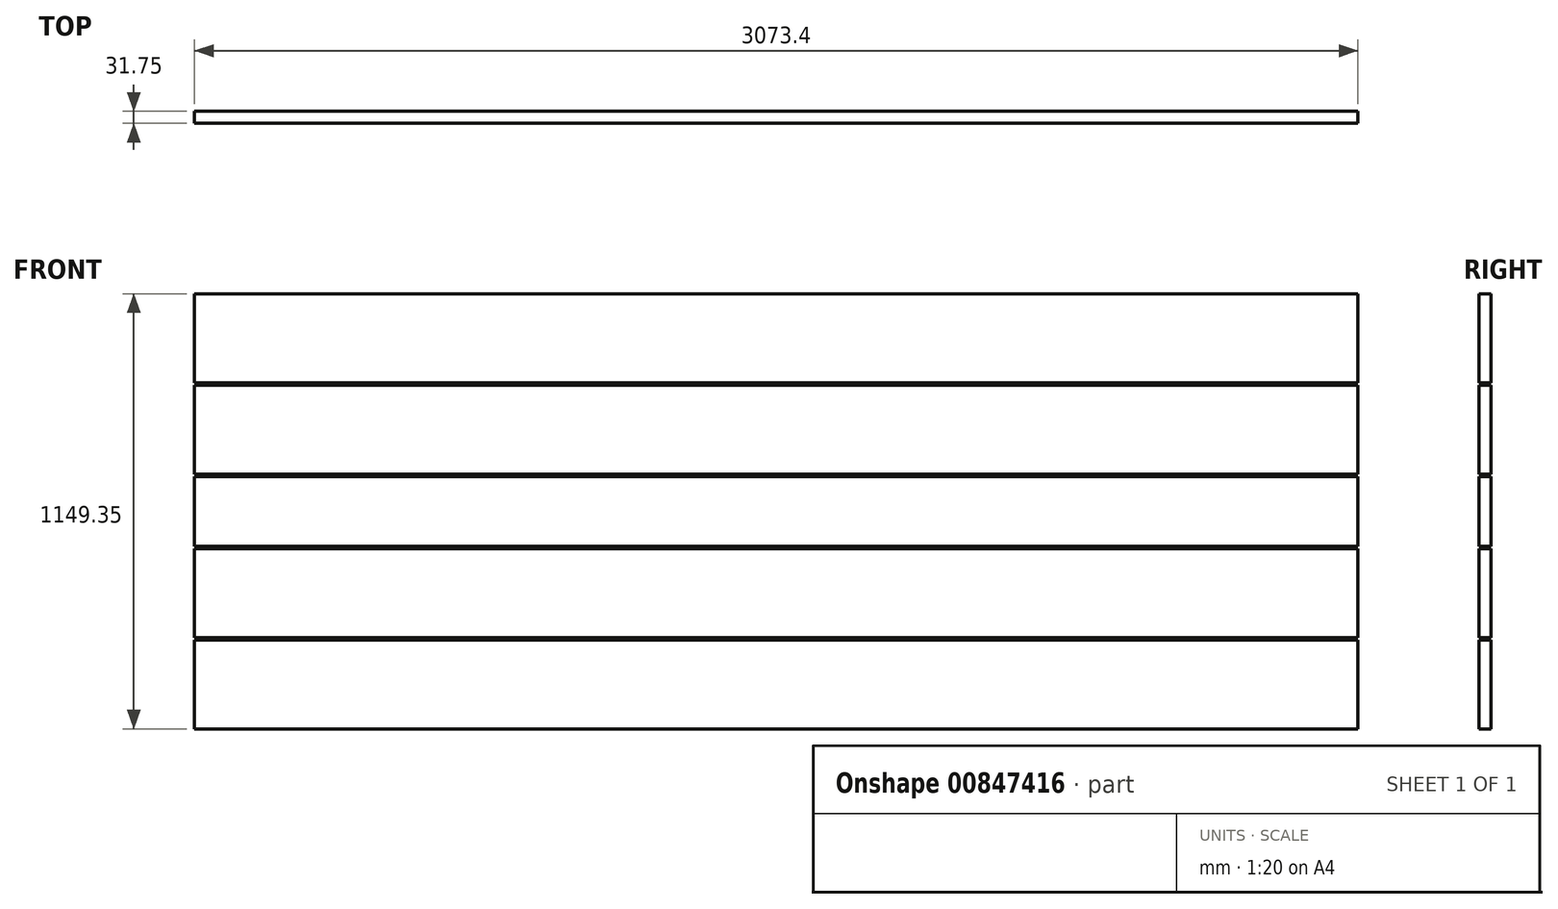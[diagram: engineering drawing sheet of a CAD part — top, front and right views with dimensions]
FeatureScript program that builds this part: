
annotation { "Feature Type Name" : "Feature", "Feature Type Description" : "" }
export const myFeature = defineFeature(function(context is Context, id is Id, definition is map)
    precondition{}
    {
        {
            var Q0;
            Q0=qCreatedBy(makeId("Front.planeOp"),FACE);
            var sketch = newSketch(context, id + "F0", { "sketchPlane" : qUnion([Q0])});
            skLineSegment(sketch, "E0.bottom", {"start": v(-1566.7, 61.16) * mm, "end": v(1506.7, 61.16) * mm});
            skLineSegment(sketch, "E0.top", {"start": v(-1566.7, -122.99) * mm, "end": v(1506.7, -122.99) * mm});
            skLineSegment(sketch, "E0.left", {"start": v(-1566.7, 61.16) * mm, "end": v(-1566.7, -122.99) * mm});
            skLineSegment(sketch, "E0.right", {"start": v(1506.7, 61.16) * mm, "end": v(1506.7, -122.99) * mm});
            skLineSegment(sketch, "E1.bottom", {"start": v(-1566.7, -129.34) * mm, "end": v(1506.7, -129.34) * mm});
            skLineSegment(sketch, "E1.top", {"start": v(-1566.7, -364.29) * mm, "end": v(1506.7, -364.29) * mm});
            skLineSegment(sketch, "E1.left", {"start": v(-1566.7, -129.34) * mm, "end": v(-1566.7, -364.29) * mm});
            skLineSegment(sketch, "E1.right", {"start": v(1506.7, -129.34) * mm, "end": v(1506.7, -364.29) * mm});
            skLineSegment(sketch, "E2.bottom", {"start": v(-1566.7, -370.64) * mm, "end": v(1506.7, -370.64) * mm});
            skLineSegment(sketch, "E2.top", {"start": v(-1566.7, -605.59) * mm, "end": v(1506.7, -605.59) * mm});
            skLineSegment(sketch, "E2.left", {"start": v(-1566.7, -370.64) * mm, "end": v(-1566.7, -605.59) * mm});
            skLineSegment(sketch, "E2.right", {"start": v(1506.7, -370.64) * mm, "end": v(1506.7, -605.59) * mm});
            skLineSegment(sketch, "E3.bottom", {"start": v(-1566.7, 67.51) * mm, "end": v(1506.7, 67.51) * mm});
            skLineSegment(sketch, "E3.top", {"start": v(-1566.7, 302.46) * mm, "end": v(1506.7, 302.46) * mm});
            skLineSegment(sketch, "E3.left", {"start": v(-1566.7, 67.51) * mm, "end": v(-1566.7, 302.46) * mm});
            skLineSegment(sketch, "E3.right", {"start": v(1506.7, 67.51) * mm, "end": v(1506.7, 302.46) * mm});
            skLineSegment(sketch, "E4.bottom", {"start": v(-1566.7, 308.81) * mm, "end": v(1506.7, 308.81) * mm});
            skLineSegment(sketch, "E4.top", {"start": v(-1566.7, 543.76) * mm, "end": v(1506.7, 543.76) * mm});
            skLineSegment(sketch, "E4.left", {"start": v(-1566.7, 308.81) * mm, "end": v(-1566.7, 543.76) * mm});
            skLineSegment(sketch, "E4.right", {"start": v(1506.7, 308.81) * mm, "end": v(1506.7, 543.76) * mm});
            skSolve(sketch);
        }
        {
            var Q0;
            Q0 = qSketchRegion(id + "F0", true);
            extrude(context, id + "F1", {"entities" : qUnion([Q0]), "depth" : 31.75 * mm, "offsetDistance" : 25.4 * mm});
        }
    });
